# Revit family: Franke_Kühleinheit_SU12_EC-A600_MS_EC_A600_FM_EC_A800_FM_EC
name_source: partatom
category: Sonderausstattung
revit_build: Autodesk Revit 2015 (Build: 20140606_1530(x64)
units: mm (PartAtom-declared; Revit-internal decimal feet)

## types (2) — shared parameters
Anzahl der Nullleiter = 1
Anzahl der Schutzleiter = 1
Anzahl von Polen = 1
Aufstellgewicht = 26 kg
Bauelement = Beistellgerät Kühleinheit SU12
Baugruppenkennzeichen = Beistellgerät Kühleinheit SU12
Beschreibung = Beistellgerät Kühleinheit SU12 dient zum Aufbewahren von vorgekühlter Milch
Breite = 340 mm  [stored 1.11549 ft]
Energieverlust nach DIN18873 = 0.783 kWh/24 h - 230 V
Hersteller = Franke
Höhe = 586 mm  [stored 1.92257 ft]
Milchvorrat = 12 l
Modell = 410874 - Kühleinheit SU12 EC - A600 MS EC, A600 FM EC, A800 FM EC
Netzfrequenz = 50 Hz
Netzfrequenz alternativ = 60 Hz
Sicherung = 10 A
Spannung = 230 V
Stromaufnahme = 0.72 A
Temperaturbreich = + 3° C bis +8° C
Tiefe = 475 mm  [stored 1.5584 ft]
URL = http://www.franke.com
zero-valued in all types: Kosten

## per-type parameters (varying)
| type | Abdeckung |
| Kühleinheit SU12 EC-A600 MS EC,A600 FM EC,A800 FM EC(230V/black line/EU) | Franke Black |
| Kühleinheit SU12 EC-A600 MS EC,A600 FM EC,A800 FM EC(230V/anthrazit/EU) | Franke Anthrazit |

note: [stored X ft] marks values corroborated as IEEE doubles in the binary element streams (Revit-internal decimal feet)
